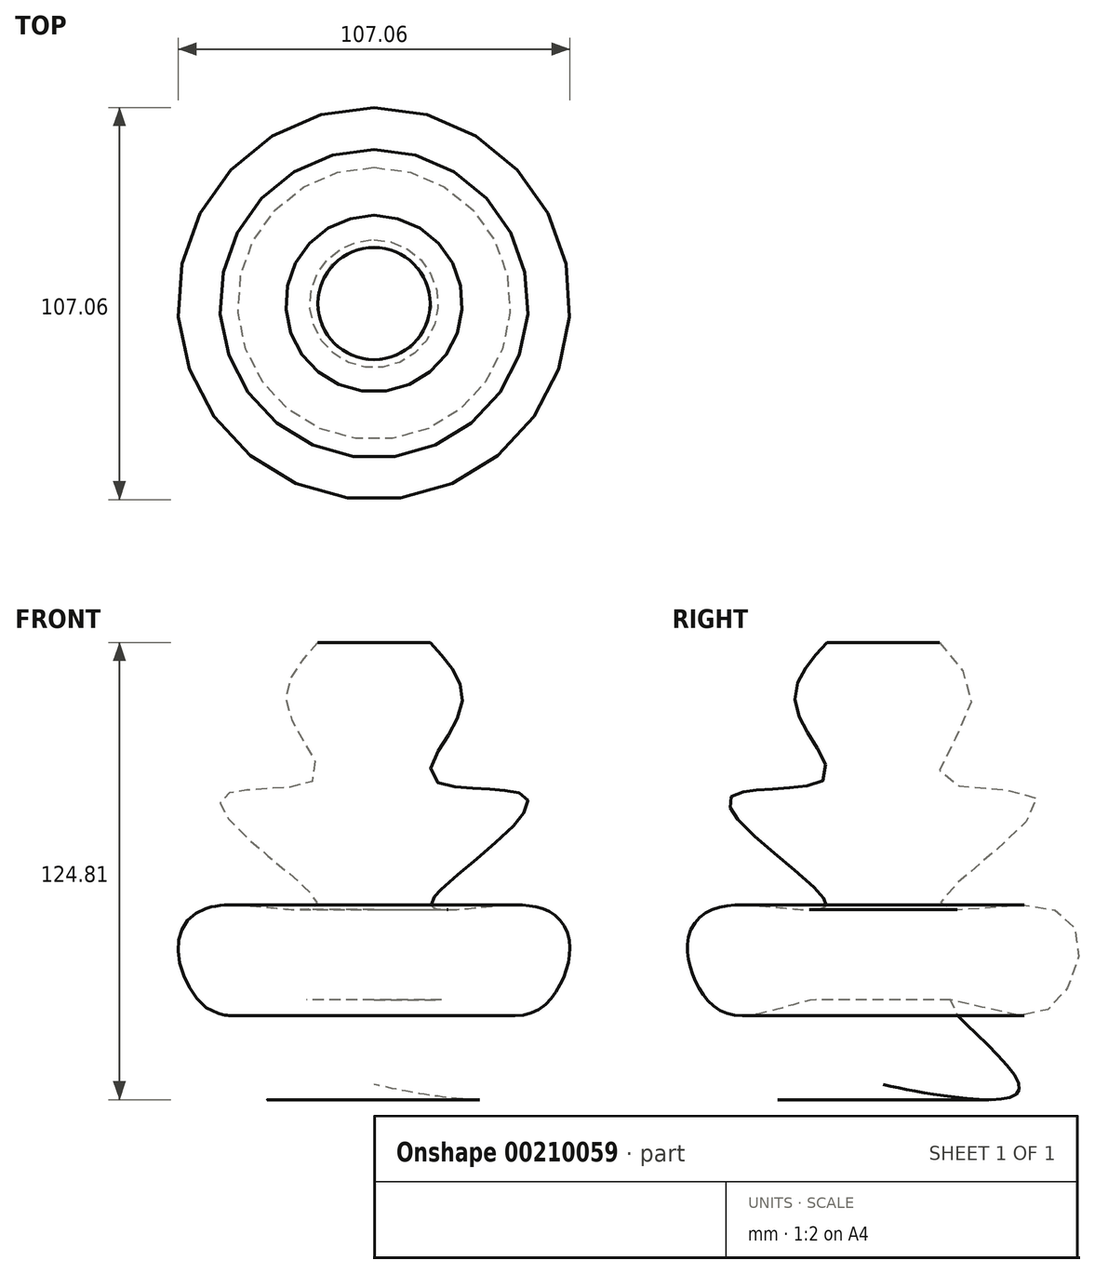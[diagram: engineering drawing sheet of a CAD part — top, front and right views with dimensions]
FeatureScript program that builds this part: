
annotation { "Feature Type Name" : "Feature", "Feature Type Description" : "" }
export const myFeature = defineFeature(function(context is Context, id is Id, definition is map)
    precondition{}
    {
        {
            var Q0;
            Q0=qCreatedBy(makeId("Right.planeOp"),FACE);
            var sketch = newSketch(context, id + "F0", { "sketchPlane" : qUnion([Q0])});
            skFitSpline(sketch, "E0", {"points": [v(15.32, 57.36) * mm, v(23.76, 39.54) * mm, v(15.94, 20.16) * mm, v(41.26, 15.47) * mm, v(30, 0) * mm, v(15.63, -14.22) * mm, v(23.44, -15.47) * mm, v(45.64, -15.16) * mm, v(53.45, -24.54) * mm, v(47.51, -40.8) * mm, v(33.45, -43.92) * mm, v(17.5, -40.8) * mm, v(37.2, -63.92) * mm, v(19.07, -66.74) * mm, v(0, -63.3) * mm], "startDerivative": vector(206.84, -221.43) * mm, "endDerivative": vector(-223.03, 50.4) * mm});
            skLineSegment(sketch, "E1", {"start": v(0, 67.05) * mm, "end": v(0, 97.06) * mm});
            skSolve(sketch);
        }
        {
            var Q0;
            Q0=sQuery(id+"F0.wireOp",EDGE,"E0");
            var Q1;
            Q1=sQuery(id+"F0.wireOp",EDGE,"E1");
            revolve(context, id + "F1", {"bodyType" : ToolBodyType.SURFACE, "surfaceEntities" : qUnion([Q0]), "axis" : qUnion([Q1]), "revolveType" : RevolveType.FULL});
        }
    });
